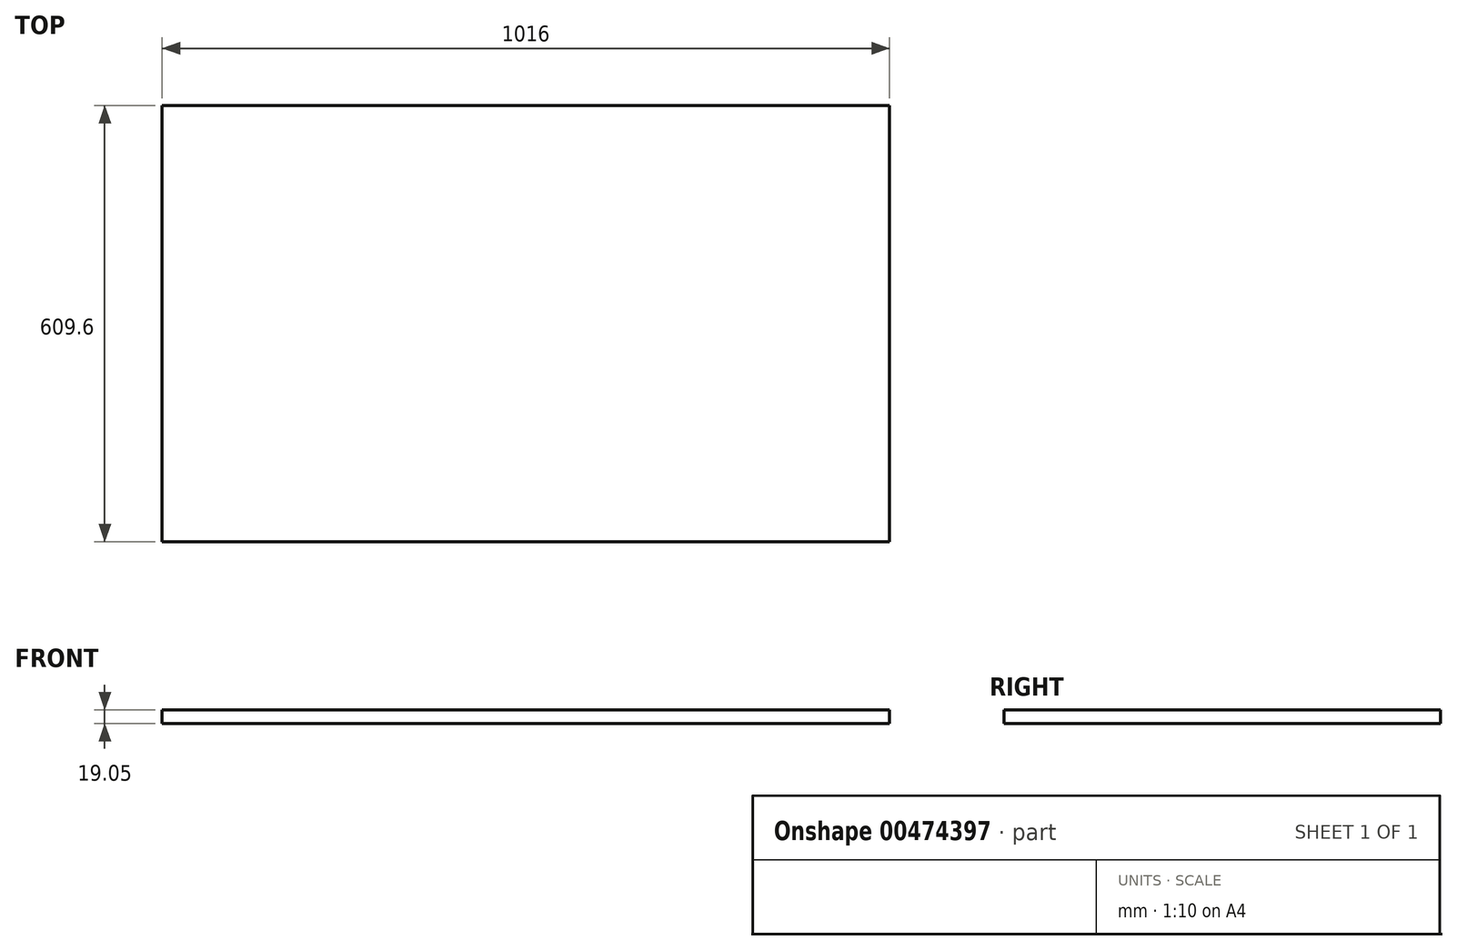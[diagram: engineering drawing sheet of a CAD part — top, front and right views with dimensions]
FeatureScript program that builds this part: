
annotation { "Feature Type Name" : "Feature", "Feature Type Description" : "" }
export const myFeature = defineFeature(function(context is Context, id is Id, definition is map)
    precondition{}
    {
        {
            var Q0;
            Q0=qCreatedBy(makeId("Top.planeOp"),FACE);
            var sketch = newSketch(context, id + "F0", { "sketchPlane" : qUnion([Q0])});
            skLineSegment(sketch, "E0.bottom", {"start": v(-508, 0) * mm, "end": v(508, 0) * mm});
            skLineSegment(sketch, "E0.top", {"start": v(-508, 609.6) * mm, "end": v(508, 609.6) * mm});
            skLineSegment(sketch, "E0.left", {"start": v(-508, 0) * mm, "end": v(-508, 609.6) * mm});
            skLineSegment(sketch, "E0.right", {"start": v(508, 0) * mm, "end": v(508, 609.6) * mm});
            skSolve(sketch);
        }
        {
            var Q0;
            Q0 = qSketchRegion(id + "F0", true);
            extrude(context, id + "F1", {"entities" : qUnion([Q0]), "oppositeDirection" : true, "depth" : 19.05 * mm});
        }
    });
